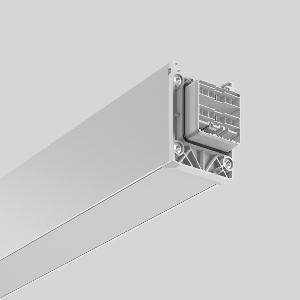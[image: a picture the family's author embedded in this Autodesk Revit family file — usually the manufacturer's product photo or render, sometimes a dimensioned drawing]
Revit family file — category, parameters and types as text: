
# Revit family: linedo_2_3m_00_0000_952300_000_400_900_132a
name_source: partatom
category: Lighting Fixtures
units: mm (PartAtom-declared; Revit-internal decimal feet)

## family parameters
Cut with Voids When Loaded = No
Host = Face
Light Source = No
Part Type = Normal
Room Calculation Point = No
Round Connector Dimension = Use Diameter
Shared = No

## types (1)
- LINEDO_2,3m_00_0000
    Apparent Load = 0 VA
    Default Elevation = 1800 mm
    Description = Series: LINEDO
Rapid-installation complete module for universal use as a continuous line luminaire. Blank module. System profile made of aluminium extrusion profile, anodised. Cover made of plastic, surface like housing. Simple, tool-free installation of system profiles using separate accessories for cable, chain or ceiling suspension. Tool-free connection and mechanical connectors to secure. Please order supply module, connection and mounting accessories separately. Luminaire with limited surface temperature in accordance with EN  60598-2-24 for use in environments in which a deposit of non-conductive dust on the luminaire can be expected. 
Colour: anodised aluminium
Length: 2310 mm
Width: 58 mm
Height: 76 mm
Weight: 4,42 kg
Type of Installation: Ceiling mounting, Suspension cable/chain
    Height = 76 mm
    Lamp = 0 x
    Length = 2291 mm
    Luminous efficacy = 0 lm/W
    Manufacturer = RZB
    ModVariant = No
    Model = 952300.000.400.900
    Mounting Place = Ceiling
    Mounting Type = Surface mounted, Pendant
    Number of Poles = 1
    OnlyDefault = Yes
    Power Factor = 1
    Product Name = LINEDO_2,3m_00_0000
    Product group = Continuous line luminaire system Linedo IP 54
    ProductGroupID = 314
    Protection Class = Protection class I
    Protection Degree = IP 54
    RLX_Detail_Level = 1
    RLX_Emergency_Light_Flux = 0 lm
    RLX_Emergency_Type = 0
    RLX_Emergency_Type_DB = No
    RlxData = <blob elided: 31085 chars, md5=fe761a7c>
    Standby Power = 0 W
    System Light Flux = 0 lm
    System Power = 0 W
    Type Comments = Product without accessories
    Type Image = 954500.000.400.900.jpg
    URL = http://relux.com
    VarID = ---
    Voltage = 230 V
    Voltage Range = 220-240 V
    Weight = 0.00 kg
    Width = 58 mm

## geometry (parser evidence)
native form markers: Blend x4, Sweep x10
no freeform markers — native parametric forms only
